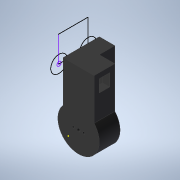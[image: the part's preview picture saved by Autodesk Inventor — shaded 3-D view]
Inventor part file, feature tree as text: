
AUTODESK INVENTOR PART (.ipt)
format: ipt  version: 2022 (Build 260153000, 153)  size: 326,144 bytes
history: native  units: in
note: dims shown in document units (in); Inventor stores cm internally (conversion verified against a paired STEP export)
features: sketch x29, extrude x23, chamfer x1
ambient origin geometry x8: Origin, YZ Plane, XZ Plane, XY Plane, X Axis, Y Axis, Z Axis, Center Point
bodies: Solid1 (feature_tree)
feature tree (53):
  extrude  "Extrusion1"  Depth=0.7874in
  extrude  "Extrusion2"  Depth=1.1811in
  extrude  "Extrusion3"  Depth=0.7874in
  extrude  "Extrusion4"  Depth=0.2362in
  extrude  "Extrusion5"  Depth=0.2362in
  extrude  "Extrusion6"  Depth=0.9055in TaperAngle=0.0deg
  extrude  "Extrusion7"  Depth=0.189in
  extrude  "Extrusion8"  Depth=0.6299in TaperAngle=0.0deg
  sketch  "Sketch11"  dims[d24=0.0984in d25=0.0591in]
  extrude  "Extrusion9"  Depth=0.0591in
  extrude  "Extrusion10"  Depth=0.0591in
  extrude  "Extrusion11"  Depth=0.3937in
  extrude  "Extrusion12"  Depth=0.1969in
  extrude  "Extrusion13"  Depth=0.1969in TaperAngle=0.0deg
  extrude  "Extrusion15"  Depth=0.1181in
  extrude  "Extrusion16"  Depth=0.1181in
  extrude  "Extrusion17"  Depth=0.3937in TaperAngle=0.0deg
  extrude  "Extrusion18"  Depth=0.3937in
  chamfer  "Chamfer2"  Distance=2.3469in
  sketch  "Sketch22"  dims[d51=0.3937in d52=0.0in d53=0.3937in d54=0.0in]
  sketch  "Sketch25"  dims[d56=0.9843in d57=0.3937in d58=0.0in]
  sketch  "Sketch29"  dims[d59=0.3937in d60=0.0in d70=0.6299in d71=0.0in]
  extrude  "Extrusion27"  Depth=0.3937in TaperAngle=0.0deg
  sketch  "Sketch34"  dims[d75=1.1826in d76=0.0in d77=0.0787in]
  sketch  "Sketch37"  dims[d78=0.0787in d79=5.4424in d80=0.0in]
  sketch  "Sketch38"  dims[d81=0.315in d82=0.0787in d83=45.0deg]
  extrude  "Extrusion31"  Depth=0.3937in TaperAngle=0.0deg
  extrude  "Extrusion32"  Depth=0.6299in TaperAngle=0.0deg
  extrude  "Extrusion33"  Depth=0.6299in TaperAngle=0.0deg
  extrude  "Extrusion34"  Depth=0.0787in
  extrude  "Extrusion35"  Depth=5.4424in TaperAngle=0.0deg
  sketch  "Sketch1"  dims[d0=0.7874in d1=1.5748in]
  sketch  "Sketch2"  dims[d2=1.1811in d3=1.9685in]
  sketch  "Sketch4"  dims[d4=0.7874in d5=0.0in d6=0.7874in]
  sketch  "Sketch6"  dims[d7=0.5906in d8=0.0in d13=0.2362in]
  sketch  "Sketch7"  dims[d14=0.9843in d15=0.2362in]
  sketch  "Sketch8"  dims[d16=0.9055in d17=0.9055in d18=0.0in]
  sketch  "Sketch9"  dims[d19=0.4724in d20=0.189in]
  sketch  "Sketch10"  dims[d21=0.189in d22=0.6299in d23=0.0in]
  sketch  "Sketch12"  dims[d26=0.0984in d27=0.0591in]
  sketch  "Sketch13"  dims[d28=0.315in d29=0.0in d30=0.3937in]
  sketch  "Sketch15"  dims[d31=0.315in d32=0.1969in]
  sketch  "Sketch16"  dims[d33=0.1969in d34=0.6225in d35=0.0in]
  sketch  "Sketch18"  dims[d36=0.0787in d37=0.1181in]
  sketch  "Sketch19"  dims[d38=0.1181in d39=0.1181in]
  sketch  "Sketch20"  dims[d40=0.315in d41=0.0in d45=0.3937in d46=0.0in]
  sketch  "Sketch21"  dims[d47=0.5906in d48=0.3937in d49=2.3469in d50=0.0in]
  sketch  "Sketch33"  dims[d72=0.7874in d73=0.6299in d74=0.0in]
  sketch  "Sketch41"  dims[d92=0.6299in]
  sketch  "Sketch42"  dims[d93=0.6299in]
  sketch  "Sketch43"  dims[d94=0.6299in]
  sketch  "Sketch44"  dims[d99=0.9843in]
  sketch  "Sketch45"  dims[d110=0.3937in d111=0.315in d112=0.2756in d113=0.0in d122=1.4188in d123=0.0in d124=0.1969in d125=0.0in d126=0.3937in d127=0.0in d128=0.6299in d129=0.7087in d130=0.6299in d131=0.1969in d132=0.2362in d133=0.0in d134=0.2756in d135=0.0in]
